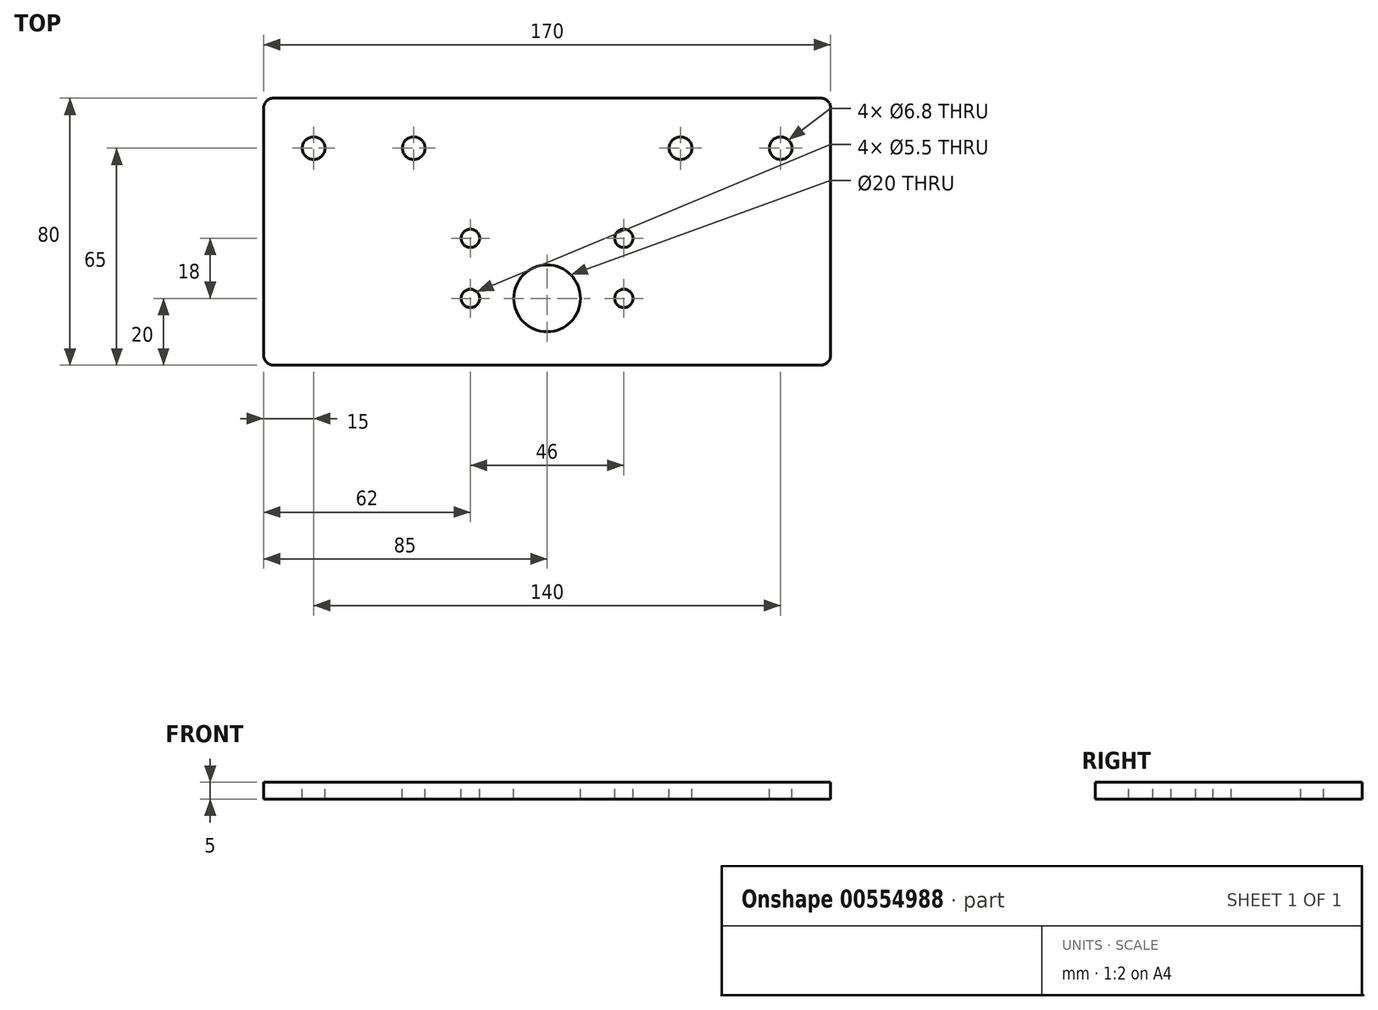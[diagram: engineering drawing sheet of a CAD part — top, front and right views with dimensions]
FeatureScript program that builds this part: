
annotation { "Feature Type Name" : "Feature", "Feature Type Description" : "" }
export const myFeature = defineFeature(function(context is Context, id is Id, definition is map)
    precondition{}
    {
        {
            var Q0;
            Q0=qCreatedBy(makeId("Top.planeOp"),FACE);
            var sketch = newSketch(context, id + "F0", { "sketchPlane" : qUnion([Q0])});
            skLineSegment(sketch, "E0.bottom", {"start": v(85, 40) * mm, "end": v(-85, 40) * mm});
            skLineSegment(sketch, "E0.top", {"start": v(85, -40) * mm, "end": v(-85, -40) * mm});
            skLineSegment(sketch, "E0.left", {"start": v(85, 40) * mm, "end": v(85, -40) * mm});
            skLineSegment(sketch, "E0.right", {"start": v(-85, 40) * mm, "end": v(-85, -40) * mm});
            skPoint(sketch, "E0.middle", {"position": v(0, 0) * mm});
            skSolve(sketch);
        }
        {
            var Q0;
            Q0 = qSketchRegion(id + "F0", true);
            extrude(context, id + "F1", {"entities" : qUnion([Q0]), "endBound" : BoundingType.SYMMETRIC, "depth" : 5 * mm, "offsetDistance" : 25 * mm});
        }
        {
            var Q0;
            Q0=makeQuery(id+"F1.opExtrude","CAP_FACE",FACE,{"disambiguationData":[OSD([sQuery(id+"F0.wireOp",EDGE,"E0.bottom"),sQuery(id+"F0.wireOp",EDGE,"E0.top"),sQuery(id+"F0.wireOp",EDGE,"E0.left"),sQuery(id+"F0.wireOp",EDGE,"E0.right")])],"isStart":false});
            var sketch = newSketch(context, id + "F2", { "sketchPlane" : qUnion([Q0])});
            skCircle(sketch, "E1", {"center": v(40, 25) * mm, "radius": 3.4 * mm});
            skCircle(sketch, "E2", {"center": v(70, 25) * mm, "radius": 3.4 * mm});
            skCircle(sketch, "E3.MirrorC", {"center": v(-40, 25) * mm, "radius": 3.4 * mm});
            skCircle(sketch, "E4.MirrorC", {"center": v(-70, 25) * mm, "radius": 3.4 * mm});
            skCircle(sketch, "E5", {"center": v(0, -20) * mm, "radius": 10 * mm});
            skCircle(sketch, "E6", {"center": v(-23, -20) * mm, "radius": 2.75 * mm});
            skCircle(sketch, "E7", {"center": v(-23, -2) * mm, "radius": 2.75 * mm});
            skCircle(sketch, "E8", {"center": v(23, -2) * mm, "radius": 2.75 * mm});
            skCircle(sketch, "E9", {"center": v(23, -20) * mm, "radius": 2.75 * mm});
            skSolve(sketch);
        }
        {
            var Q0;
            Q0 = qSketchRegion(id + "F2", true);
            extrude(context, id + "F3", {"entities" : qUnion([Q0]), "operationType" : NewBodyOperationType.REMOVE, "oppositeDirection" : true, "depth" : 5 * mm, "offsetDistance" : 25 * mm});
        }
        {
            var Q0;
            Q0=makeQuery(id+"F1.opExtrude","SWEPT_EDGE",EDGE,{"disambiguationData":[OSD([sQuery(id+"F0.wireOp",EDGE,"E0.top"),sQuery(id+"F0.wireOp",EDGE,"E0.right")])]});
            var Q1;
            Q1=makeQuery(id+"F1.opExtrude","SWEPT_EDGE",EDGE,{"disambiguationData":[OSD([sQuery(id+"F0.wireOp",EDGE,"E0.top"),sQuery(id+"F0.wireOp",EDGE,"E0.left")])]});
            var Q2;
            Q2=makeQuery(id+"F1.opExtrude","SWEPT_EDGE",EDGE,{"disambiguationData":[OSD([sQuery(id+"F0.wireOp",EDGE,"E0.bottom"),sQuery(id+"F0.wireOp",EDGE,"E0.right")])]});
            var Q3;
            Q3=makeQuery(id+"F1.opExtrude","SWEPT_EDGE",EDGE,{"disambiguationData":[OSD([sQuery(id+"F0.wireOp",EDGE,"E0.bottom"),sQuery(id+"F0.wireOp",EDGE,"E0.left")])]});
            fillet(context, id + "F4", {"entities" : qUnion([Q0, Q1, Q2, Q3]), "radius" : 3 * mm, "tangentPropagation" : true, "allowEdgeOverflow" : false});
        }
    });
